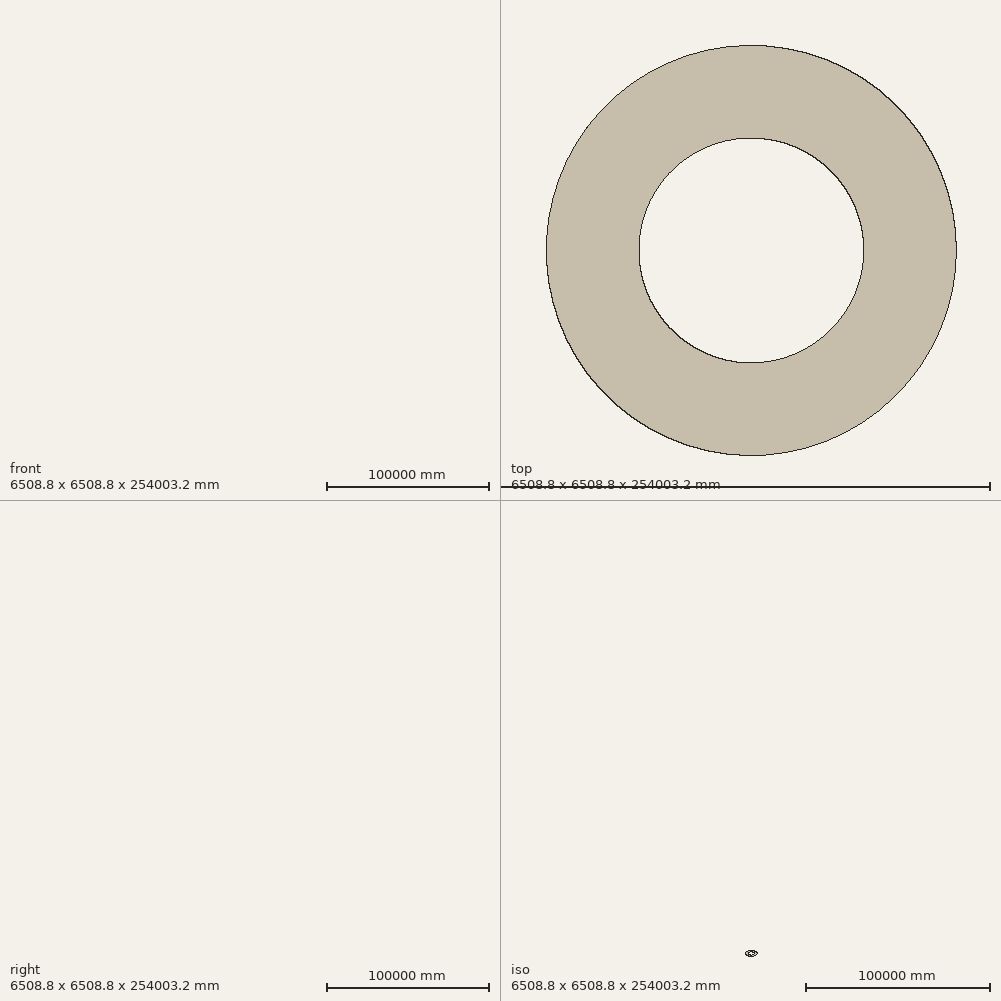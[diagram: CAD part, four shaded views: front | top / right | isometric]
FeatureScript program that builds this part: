
annotation { "Feature Type Name" : "Feature", "Feature Type Description" : "" }
export const myFeature = defineFeature(function(context is Context, id is Id, definition is map)
    precondition{}
    {
        {
            var Q0;
            Q0=qCreatedBy(makeId("Front.planeOp"),FACE);
            var sketch = newSketch(context, id + "F0", { "sketchPlane" : qUnion([Q0])});
            skLineSegment(sketch, "E0", {"start": v(0, 42.11) * mm, "end": v(0, -40.65) * mm, "construction": true});
            skSolve(sketch);
        }
        {
            var Q0;
            Q0=qCreatedBy(makeId("Front.planeOp"),FACE);
            var sketch = newSketch(context, id + "F1", { "sketchPlane" : qUnion([Q0])});
            skCircle(sketch, "E1", {"center": v(1778, 0) * mm, "radius": 3.18 * mm});
            skCircle(sketch, "E2", {"center": v(3251.2, 0) * mm, "radius": 3.18 * mm});
            skLineSegment(sketch, "E3", {"start": v(1781.18, 0) * mm, "end": v(3248.03, 0) * mm});
            skLineSegment(sketch, "E4", {"start": v(3248.03, -0.11) * mm, "end": v(1781.17, -0.11) * mm});
            skSolve(sketch);
        }
        {
            var Q0;
            Q0 = qSketchRegion(id + "F1", true);
            var Q1;
            Q1=sQuery(id+"F0.wireOp",EDGE,"E0");
            revolve(context, id + "F2", {"surfaceOperationType" : NewSurfaceOperationType.NEW, "entities" : qUnion([Q0]), "axis" : qUnion([Q1]), "revolveType" : RevolveType.FULL});
        }
        {
            var Q0;
            Q0=qCreatedBy(makeId("Top.planeOp"),FACE);
            var sketch = newSketch(context, id + "F3", { "sketchPlane" : qUnion([Q0])});
            skLineSegment(sketch, "E5", {"start": v(0, 3299.76) * mm, "end": v(0, -3567.15) * mm, "construction": true});
            skCircle(sketch, "E6", {"center": v(0, -3232.02) * mm, "radius": 5.86 * mm});
            skCircle(sketch, "E7.1.0", {"center": v(2799.01, 1616.01) * mm, "radius": 5.86 * mm});
            skCircle(sketch, "E7.2.0", {"center": v(-2799.01, 1616.01) * mm, "radius": 5.86 * mm});
            skPoint(sketch, "E7.center", {"position": v(0, 0) * mm});
            skSolve(sketch);
        }
        {
            var Q0;
            Q0 = qSketchRegion(id + "F3", true);
            extrude(context, id + "F4", {"entities" : qUnion([Q0]), "operationType" : NewBodyOperationType.ADD, "depth" : 254000 * mm, "offsetDistance" : 25.4 * mm});
        }
    });
